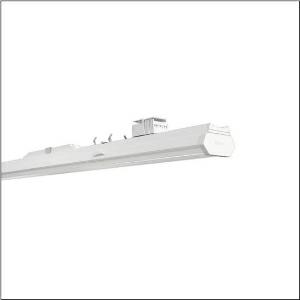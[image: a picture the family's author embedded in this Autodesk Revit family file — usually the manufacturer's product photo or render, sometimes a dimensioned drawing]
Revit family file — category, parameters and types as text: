
# Revit family: licross_r__11_protected_ho_51td11mn4gxs_4279
name_source: partatom
category: Lighting Fixtures
units: mm (PartAtom-declared; Revit-internal decimal feet)

## family parameters
Cut with Voids When Loaded = No
Host = Face
Light Source = No
Part Type = Normal
Room Calculation Point = No
Round Connector Dimension = Use Diameter
Shared = No

## types (1)
- --- (1 x LED, 16070 lm, 87.4 W, 4000K)
    Apparent Load = 87 VA
    CIE Flux Codes = 84 94 98 99 100
    Color Rendering = 80
    Color Temperature = 4000K
    Default Elevation = 1800 mm
    Description = Licross® 11 Protected HO, luminaire insert, of sheet steel, galvanised, coil coated, white, length: 1.500mm, width: 90mm, height: 101mm, LED rated luminous flux: 16.070lm, light colour: 840, control gear: ON/OFF Multilumen, control gear: ECG Multilumen, with plug, 3-pole, with phase selection, mains connection: 220..240V, AC, 50/60Hz, halogen-free wiring, primary light control with lens, of plastic, primary optical cover: cover, of PMMA, light emission: direct with ceiling illumination distribution, primary light characteristic: symmetric, protection rating (complete): IP54, insulation class (complete): insulation class I (protective earthing), certification: CE, ENEC, VDE, UKCA, protection symbol: D if used in an environment with non-conductive dust loads with corresponding accessories, impact resistance: IK06, permissible ambient temperature for indoor applications: -35..+35°C, corresponds to IFS (International Featured Standards) requirements for safety and quality in the food industry, reducing of maximum allowable ambient temperature of 5°C with ceiling mounting, LABS conformity tested according to VDMA 24364:2018-05, packaging unit: 1 piece
    Height = 92 mm
    Lamp = 1 x LED
    Lamp Light Flux = 16070 lm
    Lamp Power = 87.4 W
    Lamp count = 1
    Length = 1500 mm
    Luminous efficacy = 184 lm/W
    Manufacturer = Siteco
    ModVariant = No
    Model = 51TD11MN4GXS
    Mounting Place = Ceiling
    Mounting Type = Pendant
    Number of Poles = 1
    OnlyDefault = Yes
    Power Factor = 1
    Product Name = Licross® 11 Protected HO
    Product group = luminaire insert
    ProductGroupID = 902
    Protection Class = Protection class I
    Protection Degree = IP 54
    RLX_Detail_Level = 1
    RlxData = <blob elided: 22033 chars, md5=cdfa3236>
    Socket = socket
    Standby Power = 0 W
    System Light Flux = 16070 lm
    System Power = 87 W
    Type Comments = factory setting: luminous flux: 100 % | (A | C | E) | 203 mA
    Type Image = l_1256145.jpg
    URL = http://relux.com
    VarID = @adj_003803
    Voltage = 0 V
    Weight = 0.00 kg
    Width = 88 mm

## geometry (parser evidence)
native form markers: Blend x4, Sweep x11
no freeform markers — native parametric forms only
